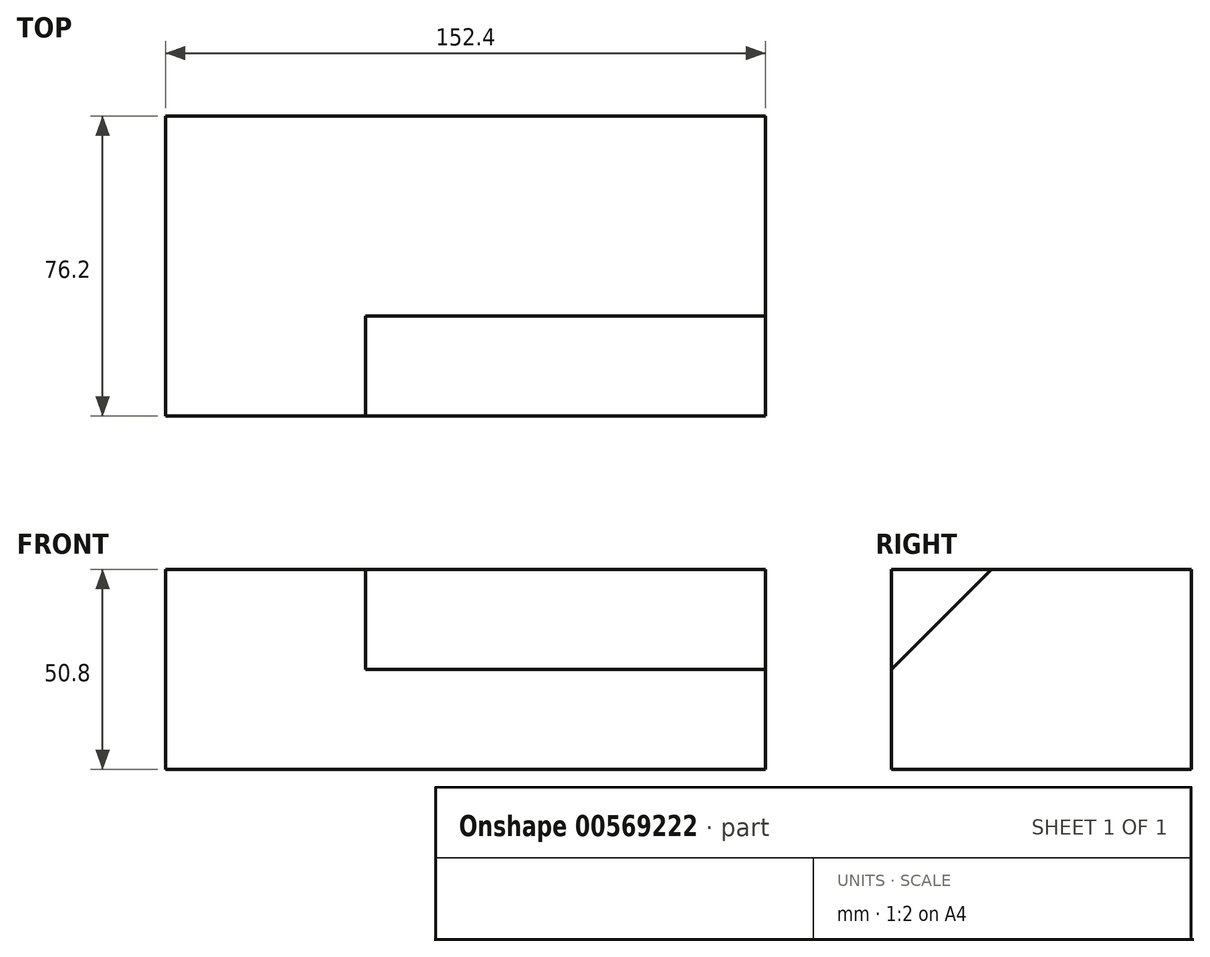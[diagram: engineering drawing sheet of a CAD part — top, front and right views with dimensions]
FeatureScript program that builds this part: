
annotation { "Feature Type Name" : "Feature", "Feature Type Description" : "" }
export const myFeature = defineFeature(function(context is Context, id is Id, definition is map)
    precondition{}
    {
        {
            var Q0;
            Q0=qCreatedBy(makeId("Right.planeOp"),FACE);
            var sketch = newSketch(context, id + "F0", { "sketchPlane" : qUnion([Q0])});
            skLineSegment(sketch, "E0.bottom", {"start": v(-49.42, 34.7) * mm, "end": v(26.78, 34.7) * mm});
            skLineSegment(sketch, "E0.top", {"start": v(-49.42, -16.1) * mm, "end": v(26.78, -16.1) * mm});
            skLineSegment(sketch, "E0.left", {"start": v(-49.42, 34.7) * mm, "end": v(-49.42, -16.1) * mm});
            skLineSegment(sketch, "E0.right", {"start": v(26.78, 34.7) * mm, "end": v(26.78, -16.1) * mm});
            skLineSegment(sketch, "E1", {"start": v(-49.42, -16.1) * mm, "end": v(-49.42, 9.3) * mm});
            skLineSegment(sketch, "E2", {"start": v(-24.02, 34.7) * mm, "end": v(26.78, 34.7) * mm});
            skLineSegment(sketch, "E3", {"start": v(-49.42, 9.3) * mm, "end": v(-24.02, 34.7) * mm});
            skSolve(sketch);
        }
        {
            var Q0;
            Q0=makeQuery(id+"F0.imprint","IMPRINT",FACE,{"disambiguationData":[TD([[makeQuery(id+"F0.imprint","IMPRINT",EDGE,{"derivedFrom":sQuery(id+"F0.wireOp",EDGE,"E0.top")}),1.0]])]});
            extrude(context, id + "F1", {"entities" : qUnion([Q0]), "depth" : 152.4 * mm, "offsetDistance" : 25.4 * mm});
        }
        {
            var Q0;
            Q0=makeQuery(id+"F0.imprint","IMPRINT",FACE,{"disambiguationData":[TD([[makeQuery(id+"F0.imprint","IMPRINT",EDGE,{"derivedFrom":sQuery(id+"F0.wireOp",EDGE,"E0.bottom")}),-1.0]])]});
            extrude(context, id + "F2", {"entities" : qUnion([Q0]), "operationType" : NewBodyOperationType.ADD, "depth" : 50.8 * mm, "offsetDistance" : 25.4 * mm});
        }
    });
